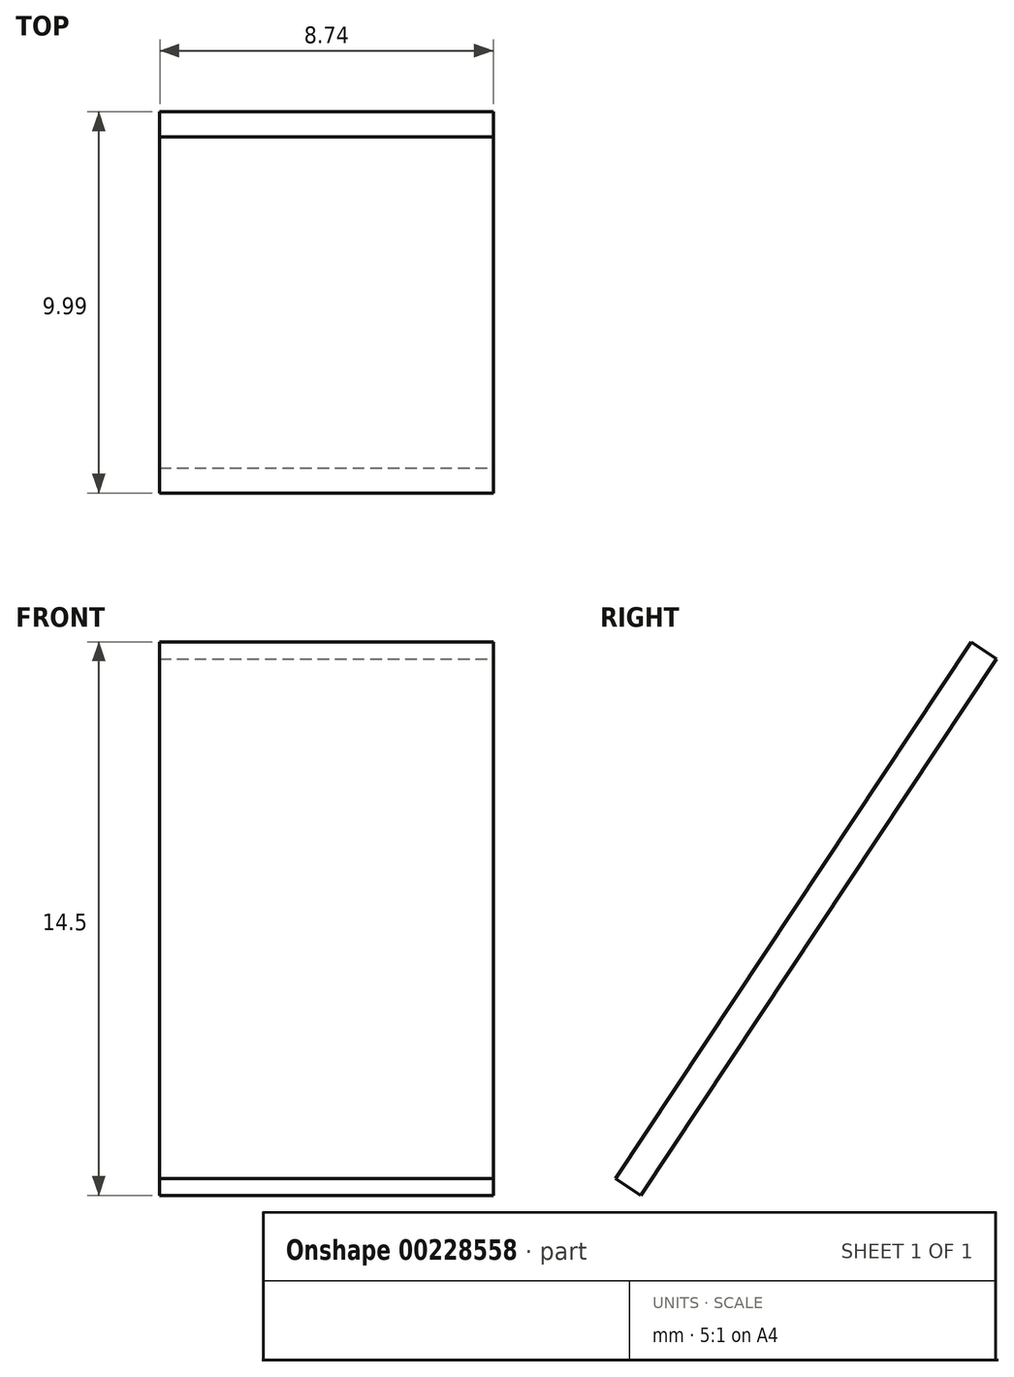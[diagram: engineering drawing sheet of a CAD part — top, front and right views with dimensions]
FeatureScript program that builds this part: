
annotation { "Feature Type Name" : "Feature", "Feature Type Description" : "" }
export const myFeature = defineFeature(function(context is Context, id is Id, definition is map)
    precondition{}
    {
        {
            var Q0;
            Q0=qCreatedBy(makeId("Right.planeOp"),FACE);
            var sketch = newSketch(context, id + "F0", { "sketchPlane" : qUnion([Q0])});
            skLineSegment(sketch, "E0", {"start": v(0, 2913.41) * mm, "end": v(-812.8, 1688.94) * mm});
            skLineSegment(sketch, "E1", {"start": v(-812.8, 1688.94) * mm, "end": v(1076.85, 1688.94) * mm, "construction": true});
            skSolve(sketch);
        }
        {
            var Q0;
            Q0=sQuery(id+"F0.wireOp",EDGE,"HXvVuCk2-IOc2-gW1W-kLZb-kXqK5PjOOn96");
            var Q1;
            Q1=sQuery(id+"F0.wireOp",EDGE,"E0");
            extrude(context, id + "F1", {"bodyType" : ToolBodyType.SURFACE, "surfaceEntities" : qUnion([Q0, Q1]), "endBound" : BoundingType.SYMMETRIC, "depth" : 762 * mm});
        }
        {
            var Q0;
            Q0=makeQuery(id+"F1.opExtrude","SWEPT_FACE",FACE,{"disambiguationData":[OSD([sQuery(id+"F0.wireOp",EDGE,"E0"),sQuery(id+"F0.wireOp",EDGE,"HXvVuCk2-IOc2-gW1W-kLZb-kXqK5PjOOn96")])]});
            extrude(context, id + "F2", {"entities" : qUnion([Q0]), "depth" : 69.14 * mm});
        }
        {
            var Q0;
            Q0=makeQuery(id+"F1.opExtrude","SWEPT_BODY",BODY,{"disambiguationData":[OSD([sQuery(id+"F0.wireOp",EDGE,"E0")])]});
            var Q1;
            Q1=makeQuery(id+"F2.opExtrude","SWEPT_BODY",BODY,{"disambiguationData":[OSD([sQuery(id+"F0.wireOp",EDGE,"E0")])]});
            var Q2;
            Q2=qCreatedBy(makeId("Origin.pointOp"),VERTEX);
            transform(context, id + "F3", {"entities" : qUnion([Q0, Q1]), "transformType" : TransformType.SCALE_UNIFORMLY, "scale" : 1 / 87.1, "scalePoint" : qUnion([Q2]), "makeCopy" : false});
        }
    });
